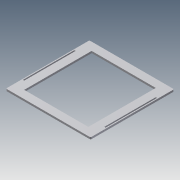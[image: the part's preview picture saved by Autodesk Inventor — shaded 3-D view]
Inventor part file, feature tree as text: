
AUTODESK INVENTOR PART (.ipt)
format: ipt  version: 2014 (Build 180170000, 170)  size: 111,616 bytes
history: native  units: mm
features: extrude x3, sketch x3, mirror x1, fillet x1
ambient origin geometry x8: Origin, YZ Plane, XZ Plane, XY Plane, X Axis, Y Axis, Z Axis, Center Point
bodies: Solid1 (feature_tree)
feature tree (8):
  extrude  "Extrusion1"  Depth=260.38625mm
  extrude  "Extrusion2"  Depth=3.0mm
  mirror  "Mirror1"
  fillet  "Fillet1"  Radius=4.0mm
  extrude  "Extrusion3"  Depth=4.0mm TaperAngle=0.0deg
  sketch  "Sketch1"  dims[d0=264.0mm d1=260.38625mm]
  sketch  "Sketch2"  dims[d2=6.0mm d3=0.0mm d5=3.0mm d6=4.0mm]
  sketch  "Sketch3"  dims[d7=50.0mm d9=4.0mm d10=0.0mm d11=3.0mm d12=25.0mm d13=25.0mm d14=4.0mm d15=0.0mm d101=50.0mm]
